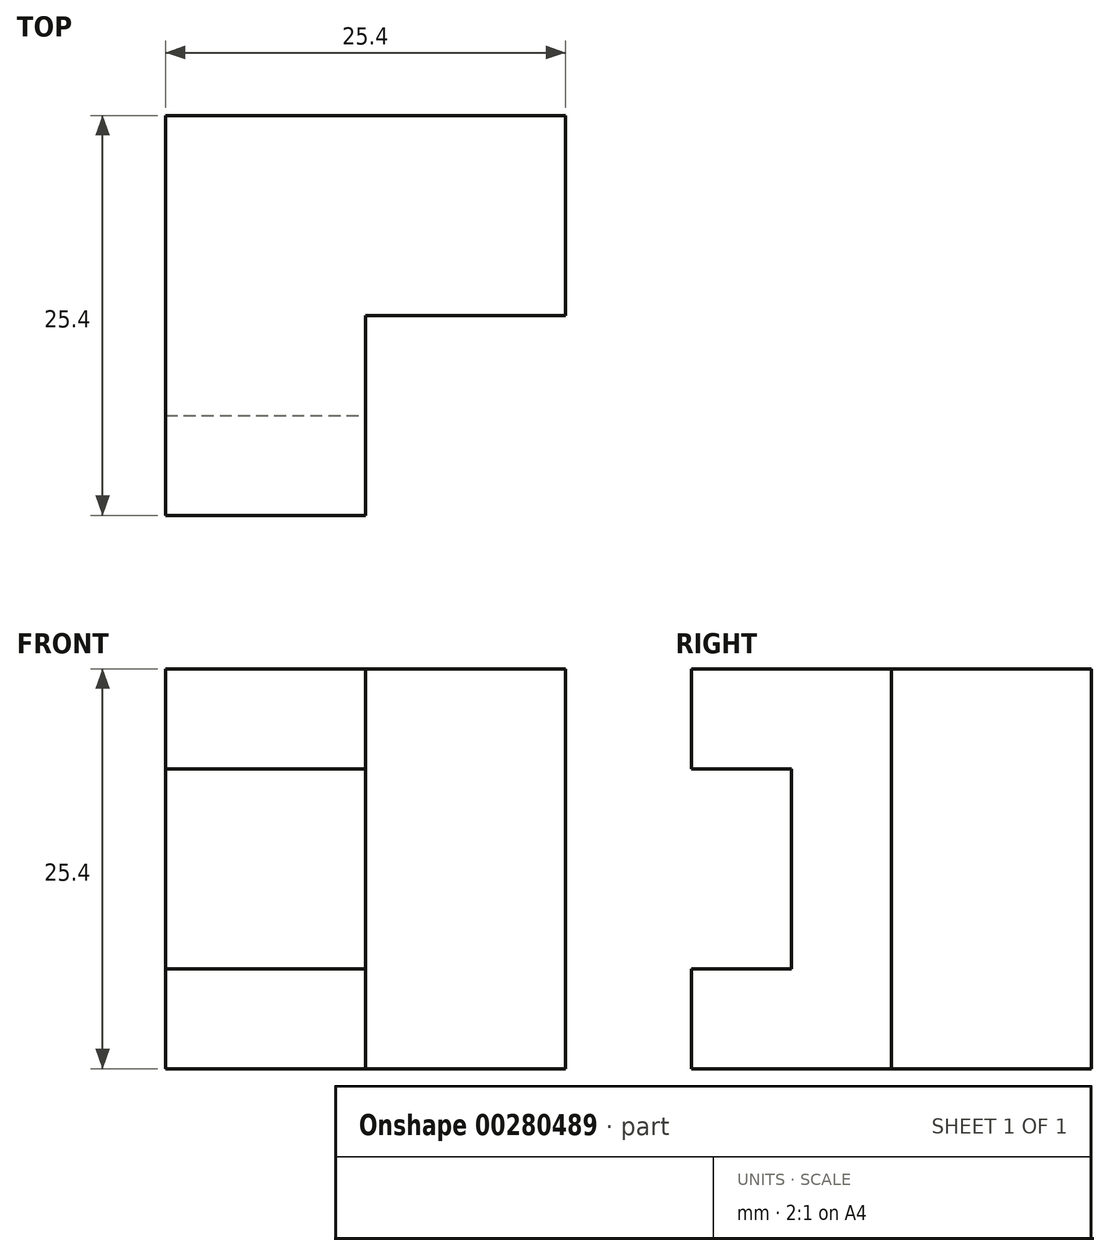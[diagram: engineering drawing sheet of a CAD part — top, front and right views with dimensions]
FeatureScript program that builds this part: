
annotation { "Feature Type Name" : "Feature", "Feature Type Description" : "" }
export const myFeature = defineFeature(function(context is Context, id is Id, definition is map)
    precondition{}
    {
        {
            var Q0;
            Q0=qCreatedBy(makeId("Front.planeOp"),FACE);
            var sketch = newSketch(context, id + "F0", { "sketchPlane" : qUnion([Q0])});
            skLineSegment(sketch, "E0.bottom", {"start": v(0, 0) * mm, "end": v(12.7, 0) * mm});
            skLineSegment(sketch, "E0.top", {"start": v(0, 25.4) * mm, "end": v(12.7, 25.4) * mm});
            skLineSegment(sketch, "E0.left", {"start": v(0, 0) * mm, "end": v(0, 25.4) * mm});
            skLineSegment(sketch, "E0.right", {"start": v(12.7, 0) * mm, "end": v(12.7, 25.4) * mm});
            skSolve(sketch);
        }
        {
            var Q0;
            Q0 = qSketchRegion(id + "F0", true);
            extrude(context, id + "F1", {"entities" : qUnion([Q0]), "oppositeDirection" : true, "depth" : 25.4 * mm});
        }
        {
            var Q0;
            Q0=makeQuery(id+"F1.opExtrude","CAP_FACE",FACE,{"disambiguationData":[OSD([sQuery(id+"F0.wireOp",EDGE,"E0.bottom"),sQuery(id+"F0.wireOp",EDGE,"E0.top"),sQuery(id+"F0.wireOp",EDGE,"E0.left"),sQuery(id+"F0.wireOp",EDGE,"E0.right")])],"isStart":true});
            var sketch = newSketch(context, id + "F2", { "sketchPlane" : qUnion([Q0])});
            skSolve(sketch);
        }
        {
            var Q0;
            Q0=makeQuery(id+"F2.imprint","IMPRINT",FACE,{"disambiguationData":[TD([[makeQuery(id+"F2.imprint","IMPRINT",EDGE,{"derivedFrom":makeQuery(id+"F1.opExtrude","CAP_EDGE",EDGE,{"disambiguationData":[OSD([sQuery(id+"F0.wireOp",EDGE,"E0.bottom")])],"isStart":true})}),1.0]])]});
            var sketch = newSketch(context, id + "F3", { "sketchPlane" : qUnion([Q0])});
            skLineSegment(sketch, "E1.bottom", {"start": v(0, 19.05) * mm, "end": v(12.7, 19.05) * mm});
            skLineSegment(sketch, "E1.top", {"start": v(0, 6.35) * mm, "end": v(12.7, 6.35) * mm});
            skLineSegment(sketch, "E1.left", {"start": v(0, 19.05) * mm, "end": v(0, 6.35) * mm});
            skLineSegment(sketch, "E1.right", {"start": v(12.7, 19.05) * mm, "end": v(12.7, 6.35) * mm});
            skSolve(sketch);
        }
        {
            var Q0;
            Q0 = qSketchRegion(id + "F3", true);
            extrude(context, id + "F4", {"entities" : qUnion([Q0]), "operationType" : NewBodyOperationType.REMOVE, "oppositeDirection" : true, "depth" : 6.35 * mm});
        }
        {
            var Q0;
            Q0=makeQuery(id+"F1.opExtrude","SWEPT_FACE",FACE,{"disambiguationData":[OSD([sQuery(id+"F0.wireOp",EDGE,"E0.right")])]});
            var sketch = newSketch(context, id + "F5", { "sketchPlane" : qUnion([Q0])});
            skLineSegment(sketch, "E2.bottom", {"start": v(25.4, 25.4) * mm, "end": v(12.7, 25.4) * mm});
            skLineSegment(sketch, "E2.top", {"start": v(25.4, 0) * mm, "end": v(12.7, 0) * mm});
            skLineSegment(sketch, "E2.left", {"start": v(25.4, 25.4) * mm, "end": v(25.4, 0) * mm});
            skLineSegment(sketch, "E2.right", {"start": v(12.7, 25.4) * mm, "end": v(12.7, 0) * mm});
            skSolve(sketch);
        }
        {
            var Q0;
            Q0 = qSketchRegion(id + "F5", true);
            extrude(context, id + "F6", {"entities" : qUnion([Q0]), "operationType" : NewBodyOperationType.ADD, "depth" : 12.7 * mm});
        }
    });
